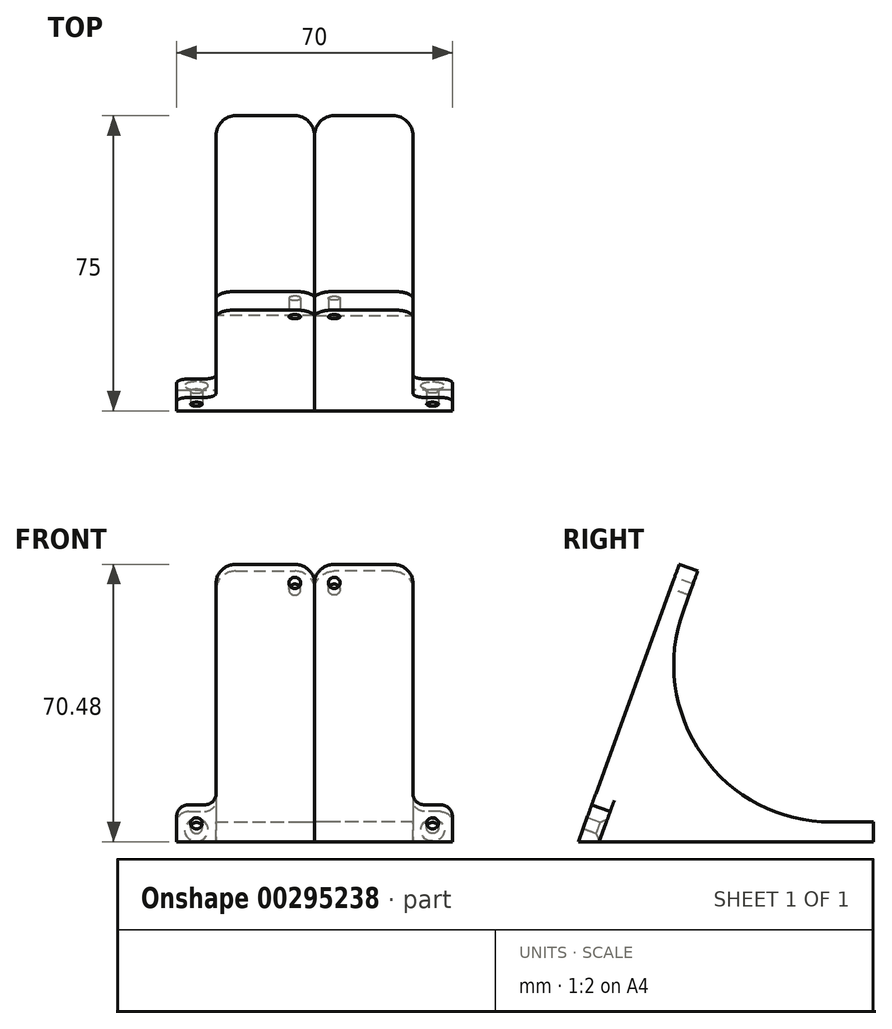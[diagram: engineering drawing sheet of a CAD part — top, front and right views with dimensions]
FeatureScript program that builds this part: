
annotation { "Feature Type Name" : "Feature", "Feature Type Description" : "" }
export const myFeature = defineFeature(function(context is Context, id is Id, definition is map)
    precondition{}
    {
        {
            var Q0;
            Q0=qCreatedBy(makeId("Right.planeOp"),FACE);
            var sketch = newSketch(context, id + "F0", { "sketchPlane" : qUnion([Q0])});
            skLineSegment(sketch, "E0", {"start": v(0, 0) * mm, "end": v(75, 0) * mm});
            skLineSegment(sketch, "E1", {"start": v(75, 0) * mm, "end": v(75, 5) * mm});
            skLineSegment(sketch, "E2", {"start": v(0, 0) * mm, "end": v(25.65, 70.48) * mm});
            skLineSegment(sketch, "E3", {"start": v(25.65, 70.48) * mm, "end": v(30.35, 68.77) * mm});
            skLineSegment(sketch, "E4", {"start": v(30.35, 68.77) * mm, "end": v(7.14, 5) * mm});
            skLineSegment(sketch, "E5", {"start": v(7.14, 5) * mm, "end": v(75, 5) * mm});
            skSolve(sketch);
        }
        {
            var Q0;
            Q0=makeQuery(id+"F0.imprint","IMPRINT",FACE,{"disambiguationData":[TD([[makeQuery(id+"F0.imprint","IMPRINT",EDGE,{"derivedFrom":sQuery(id+"F0.wireOp",EDGE,"E0")}),1.0]])]});
            extrude(context, id + "F1", {"entities" : qUnion([Q0]), "depth" : 25 * mm});
        }
        {
            var Q0;
            Q0=makeQuery(id+"F1.opExtrude","CAP_FACE",FACE,{"disambiguationData":[OSD([sQuery(id+"F0.wireOp",EDGE,"E0"),sQuery(id+"F0.wireOp",EDGE,"E1"),sQuery(id+"F0.wireOp",EDGE,"E2"),sQuery(id+"F0.wireOp",EDGE,"E3"),sQuery(id+"F0.wireOp",EDGE,"E4"),sQuery(id+"F0.wireOp",EDGE,"E5")])],"isStart":false});
            var sketch = newSketch(context, id + "F2", { "sketchPlane" : qUnion([Q0])});
            skLineSegment(sketch, "E6", {"start": v(3.42, 9.4) * mm, "end": v(8.12, 7.69) * mm});
            skLineSegment(sketch, "E7", {"start": v(7.14, 5) * mm, "end": v(5.32, 0) * mm});
            skSolve(sketch);
        }
        {
            var Q0;
            Q0 = qSketchRegion(id + "F2", true);
            var Q1;
            {var subQ3=sQuery(id+"F2.wireOp",EDGE,"E6");Q1=makeQuery(id+"F2.imprint","IMPRINT",FACE,{"disambiguationData":[TD([[makeQuery(id+"F2.imprint","IMPRINT",EDGE,{"derivedFrom":subQ3}),-1.0]])]});}
            extrude(context, id + "F3", {"entities" : qUnion([Q0, Q1]), "operationType" : NewBodyOperationType.ADD, "depth" : 10 * mm});
        }
        {
            var Q0;
            {var subQ0=sQuery(id+"F0.wireOp",EDGE,"E2");Q0=makeQuery(id+"FraU497lNe3U8tz_1.boolean.opBoolean","MERGE",FACE,{"derivedFrom":[makeQuery(id+"F3.boolean.opBoolean","MERGE",FACE,{"derivedFrom":[makeQuery(id+"F1.opExtrude","SWEPT_FACE",FACE,{"disambiguationData":[OSD([subQ0])]}),makeQuery(id+"F3.opExtrude","SWEPT_FACE",FACE,{"disambiguationData":[OSD([subQ0])]})]}),makeQuery(id+"FraU497lNe3U8tz_1.opExtrude","SWEPT_FACE",FACE,{"disambiguationData":[OSD([subQ0])]})]});}
            var sketch = newSketch(context, id + "F4", { "sketchPlane" : qUnion([Q0])});
            skCircle(sketch, "E8", {"center": v(30, 5) * mm, "radius": 1.5 * mm});
            skPoint(sketch, "E8.centerSnap0", {"position": v(30, 10) * mm});
            skPoint(sketch, "E8.centerSnap1", {"position": v(35, 5) * mm});
            skCircle(sketch, "E9", {"center": v(5, 70) * mm, "radius": 1.5 * mm});
            skSolve(sketch);
        }
        {
            var Q0;
            Q0=makeQuery(id+"F4.imprint","IMPRINT",FACE,{"disambiguationData":[TD([[makeQuery(id+"F4.imprint","IMPRINT",EDGE,{"derivedFrom":sQuery(id+"F4.wireOp",EDGE,"B2ZHbKR6-sa3T-9xf9-afnR-GZNTScDbGTRI")}),1.0]])]});
            var Q1;
            Q1=makeQuery(id+"F4.imprint","IMPRINT",FACE,{"disambiguationData":[TD([[makeQuery(id+"F4.imprint","IMPRINT",EDGE,{"derivedFrom":sQuery(id+"F4.wireOp",EDGE,"E8")}),1.0]])]});
            var Q2;
            Q2=makeQuery(id+"F4.imprint","IMPRINT",FACE,{"disambiguationData":[TD([[makeQuery(id+"F4.imprint","IMPRINT",EDGE,{"derivedFrom":sQuery(id+"F4.wireOp",EDGE,"E9")}),1.0]])]});
            extrude(context, id + "F5", {"entities" : qUnion([Q0, Q1, Q2]), "operationType" : NewBodyOperationType.REMOVE, "oppositeDirection" : true, "depth" : 25 * mm});
        }
        {
            var Q0;
            {var subQ0=sQuery(id+"F0.wireOp",EDGE,"E4");Q0=makeQuery(id+"F5.boolean.opBoolean","INTERSECT",EDGE,{"derivedFrom":[makeQuery(id+"FraU497lNe3U8tz_1.boolean.opBoolean","MERGE",FACE,{"derivedFrom":[makeQuery(id+"F3.boolean.opBoolean","MERGE",FACE,{"derivedFrom":[makeQuery(id+"F1.opExtrude","SWEPT_FACE",FACE,{"disambiguationData":[OSD([subQ0])]}),makeQuery(id+"F3.opExtrude","SWEPT_FACE",FACE,{"disambiguationData":[OSD([subQ0,sQuery(id+"F2.wireOp",EDGE,"E7")])]})]}),makeQuery(id+"FraU497lNe3U8tz_1.opExtrude","SWEPT_FACE",FACE,{"disambiguationData":[OSD([sQuery(id+"FY3Gj2LF1vKdg1Q_1.wireOp",EDGE,"YP1INpUL-SXD1-K7yZ-kv5G-Nz82jFLmzToE")])]})]}),makeQuery(id+"F5.opExtrude","SWEPT_FACE",FACE,{"disambiguationData":[OSD([sQuery(id+"F4.wireOp",EDGE,"B2ZHbKR6-sa3T-9xf9-afnR-GZNTScDbGTRI")])]})]});}
            var Q1;
            {var subQ0=sQuery(id+"F0.wireOp",EDGE,"E4");Q1=makeQuery(id+"F5.boolean.opBoolean","INTERSECT",EDGE,{"derivedFrom":[makeQuery(id+"FraU497lNe3U8tz_1.boolean.opBoolean","MERGE",FACE,{"derivedFrom":[makeQuery(id+"F3.boolean.opBoolean","MERGE",FACE,{"derivedFrom":[makeQuery(id+"F1.opExtrude","SWEPT_FACE",FACE,{"disambiguationData":[OSD([subQ0])]}),makeQuery(id+"F3.opExtrude","SWEPT_FACE",FACE,{"disambiguationData":[OSD([subQ0,sQuery(id+"F2.wireOp",EDGE,"E7")])]})]}),makeQuery(id+"FraU497lNe3U8tz_1.opExtrude","SWEPT_FACE",FACE,{"disambiguationData":[OSD([sQuery(id+"FY3Gj2LF1vKdg1Q_1.wireOp",EDGE,"YP1INpUL-SXD1-K7yZ-kv5G-Nz82jFLmzToE")])]})]}),makeQuery(id+"F5.opExtrude","SWEPT_FACE",FACE,{"disambiguationData":[OSD([sQuery(id+"F4.wireOp",EDGE,"E8")])]})]});}
            chamfer(context, id + "F6", {"entities" : qUnion([Q0, Q1]), "width" : 1.5 * mm, "tangentPropagation" : true});
        }
        {
            var Q0;
            Q0=makeQuery(id+"F1.opExtrude","SWEPT_EDGE",EDGE,{"disambiguationData":[OSD([sQuery(id+"F0.wireOp",EDGE,"E4"),sQuery(id+"F0.wireOp",EDGE,"E5")])]});
            fillet(context, id + "F7", {"entities" : qUnion([Q0]), "radius" : 40 * mm, "tangentPropagation" : true, "allowEdgeOverflow" : false});
        }
        {
            var Q0;
            Q0=makeQuery(id+"F1.opExtrude","CAP_EDGE",EDGE,{"disambiguationData":[OSD([sQuery(id+"F0.wireOp",EDGE,"E3")])],"isStart":false});
            var Q1;
            Q1=makeQuery(id+"F1.opExtrude","CAP_EDGE",EDGE,{"disambiguationData":[OSD([sQuery(id+"F0.wireOp",EDGE,"E3")])],"isStart":true});
            var Q2;
            Q2=makeQuery(id+"F1.opExtrude","CAP_EDGE",EDGE,{"disambiguationData":[OSD([sQuery(id+"F0.wireOp",EDGE,"E1")])],"isStart":true});
            var Q3;
            Q3=makeQuery(id+"F1.opExtrude","CAP_EDGE",EDGE,{"disambiguationData":[OSD([sQuery(id+"F0.wireOp",EDGE,"E1")])],"isStart":false});
            fillet(context, id + "F8", {"entities" : qUnion([Q0, Q1, Q2, Q3]), "radius" : 5 * mm, "tangentPropagation" : true, "allowEdgeOverflow" : false});
        }
        {
            var Q0;
            Q0=makeQuery(id+"F3.opExtrude","CAP_EDGE",EDGE,{"disambiguationData":[OSD([sQuery(id+"F2.wireOp",EDGE,"E6")])],"isStart":false});
            var Q1;
            Q1=makeQuery(id+"F3.opExtrude","CAP_EDGE",EDGE,{"disambiguationData":[OSD([sQuery(id+"F2.wireOp",EDGE,"E6")])],"isStart":true});
            var Q2;
            Q2=makeQuery(id+"FraU497lNe3U8tz_1.opExtrude","CAP_EDGE",EDGE,{"disambiguationData":[OSD([sQuery(id+"FY3Gj2LF1vKdg1Q_1.wireOp",EDGE,"xTBzIlT4-JV6E-jU2Q-pTeQ-Ws221JpyLK5x")])],"isStart":true});
            var Q3;
            Q3=makeQuery(id+"FraU497lNe3U8tz_1.opExtrude","CAP_EDGE",EDGE,{"disambiguationData":[OSD([sQuery(id+"FY3Gj2LF1vKdg1Q_1.wireOp",EDGE,"xTBzIlT4-JV6E-jU2Q-pTeQ-Ws221JpyLK5x")])],"isStart":false});
            fillet(context, id + "F9", {"entities" : qUnion([Q0, Q1, Q2, Q3]), "radius" : 3 * mm, "tangentPropagation" : true, "allowEdgeOverflow" : false});
        }
        {
            var Q0;
            Q0=makeQuery(id+"F1.opExtrude","SWEPT_BODY",BODY,{"disambiguationData":[OSD([sQuery(id+"F0.wireOp",EDGE,"E0"),sQuery(id+"F0.wireOp",EDGE,"E1"),sQuery(id+"F0.wireOp",EDGE,"E2"),sQuery(id+"F0.wireOp",EDGE,"E3"),sQuery(id+"F0.wireOp",EDGE,"E4"),sQuery(id+"F0.wireOp",EDGE,"E5")])]});
            var Q1;
            Q1=qCreatedBy(makeId("Right.planeOp"),FACE);
            mirror(context, id + "F10", {"entities" : qUnion([Q0]), "mirrorPlane" : qUnion([Q1])});
        }
    });
